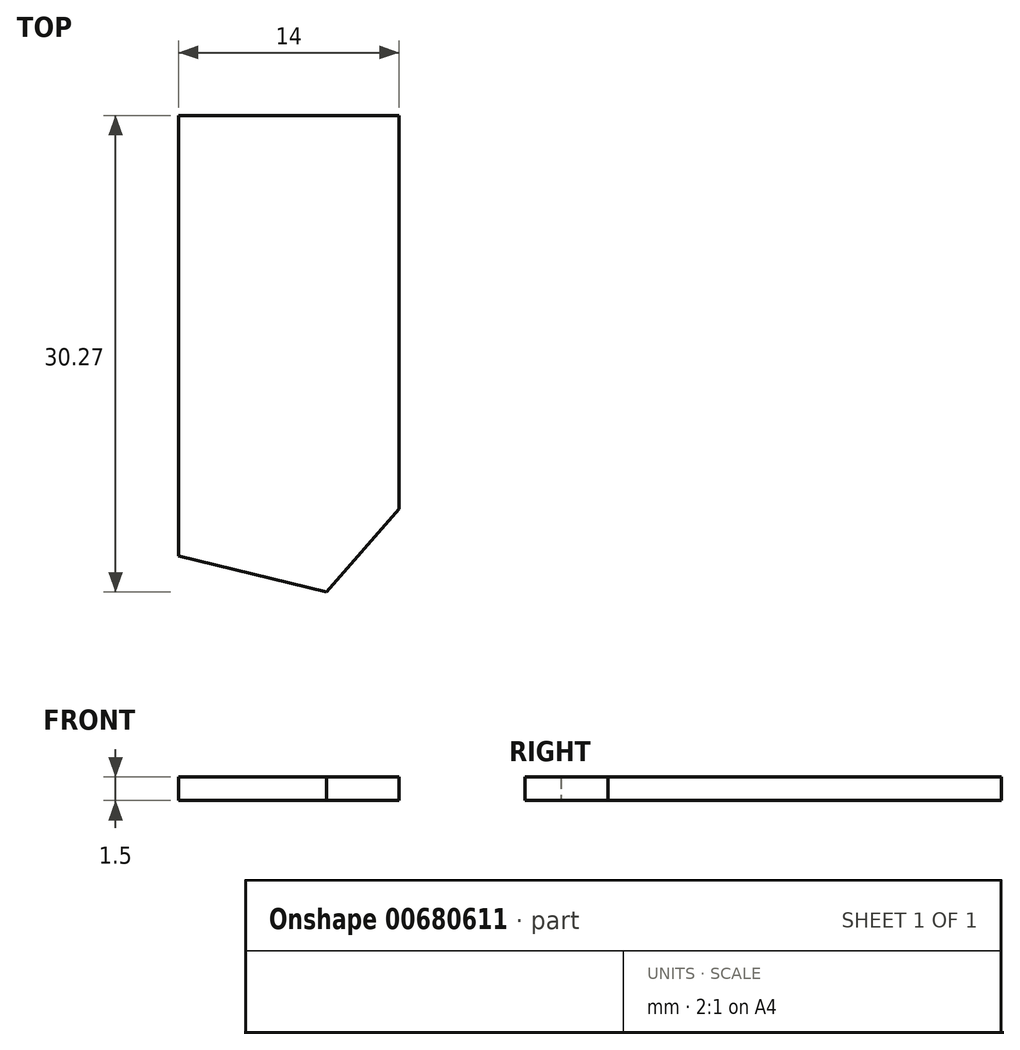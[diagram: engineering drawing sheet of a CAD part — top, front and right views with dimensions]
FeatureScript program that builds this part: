
annotation { "Feature Type Name" : "Feature", "Feature Type Description" : "" }
export const myFeature = defineFeature(function(context is Context, id is Id, definition is map)
    precondition{}
    {
        {
            var Q0;
            Q0=qCreatedBy(makeId("Top.planeOp"),FACE);
            var sketch = newSketch(context, id + "F0", { "sketchPlane" : qUnion([Q0])});
            skLineSegment(sketch, "E0", {"start": v(0, 0) * mm, "end": v(14, 0) * mm});
            skLineSegment(sketch, "E1", {"start": v(14, 0) * mm, "end": v(14, -25) * mm});
            skLineSegment(sketch, "E2", {"start": v(14, -25) * mm, "end": v(9.39, -30.27) * mm});
            skLineSegment(sketch, "E3", {"start": v(9.39, -30.27) * mm, "end": v(0, -28) * mm});
            skLineSegment(sketch, "E4", {"start": v(0, -28) * mm, "end": v(0, 0) * mm});
            skSolve(sketch);
        }
        {
            var Q0;
            Q0 = qSketchRegion(id + "F0", true);
            extrude(context, id + "F1", {"entities" : qUnion([Q0]), "depth" : 1.5 * mm, "offsetDistance" : 25 * mm});
        }
    });
